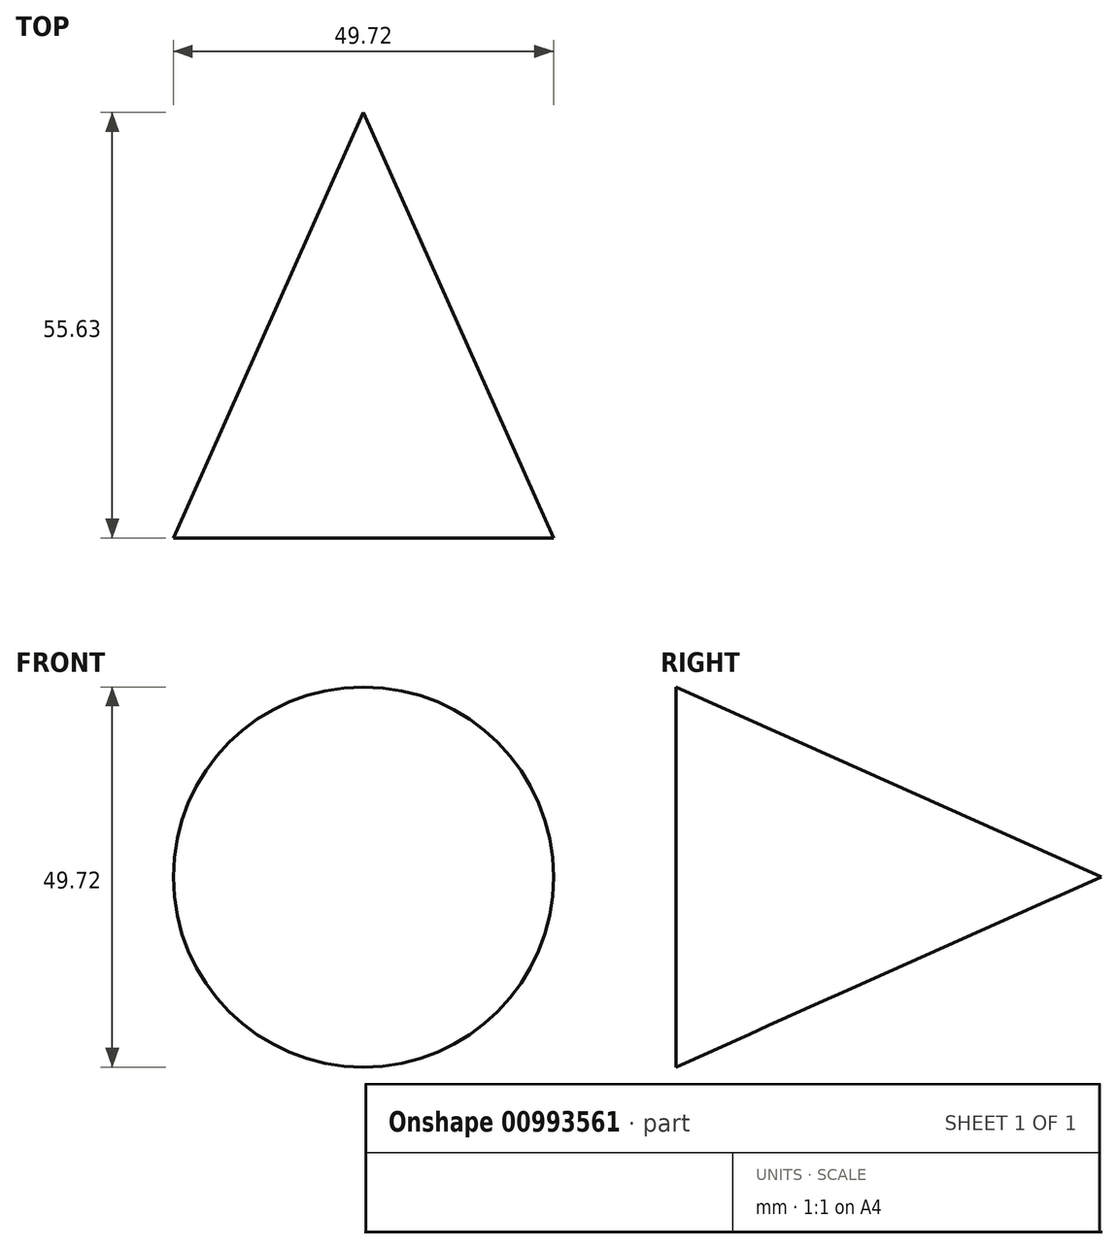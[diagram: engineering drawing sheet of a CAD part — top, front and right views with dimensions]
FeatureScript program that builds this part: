
annotation { "Feature Type Name" : "Feature", "Feature Type Description" : "" }
export const myFeature = defineFeature(function(context is Context, id is Id, definition is map)
    precondition{}
    {
        {
            var Q0;
            Q0=qCreatedBy(makeId("Top.planeOp"),FACE);
            var sketch = newSketch(context, id + "F0", { "sketchPlane" : qUnion([Q0])});
            skLineSegment(sketch, "E0", {"start": v(0, 55.63) * mm, "end": v(24.86, 0) * mm});
            skLineSegment(sketch, "E1", {"start": v(24.86, 0) * mm, "end": v(0, 0) * mm});
            skLineSegment(sketch, "E2", {"start": v(0, 67.56) * mm, "end": v(0, -13.8) * mm, "construction": true});
            skSolve(sketch);
        }
        {
            var Q0;
            Q0=sQuery(id+"F0.wireOp",EDGE,"E0");
            var Q1;
            Q1=sQuery(id+"F0.wireOp",EDGE,"E1");
            var Q2;
            Q2=sQuery(id+"F0.wireOp",EDGE,"E2");
            revolve(context, id + "F1", {"bodyType" : ToolBodyType.SURFACE, "surfaceOperationType" : NewSurfaceOperationType.NEW, "surfaceEntities" : qUnion([Q0, Q1]), "axis" : qUnion([Q2]), "revolveType" : RevolveType.FULL});
        }
    });
